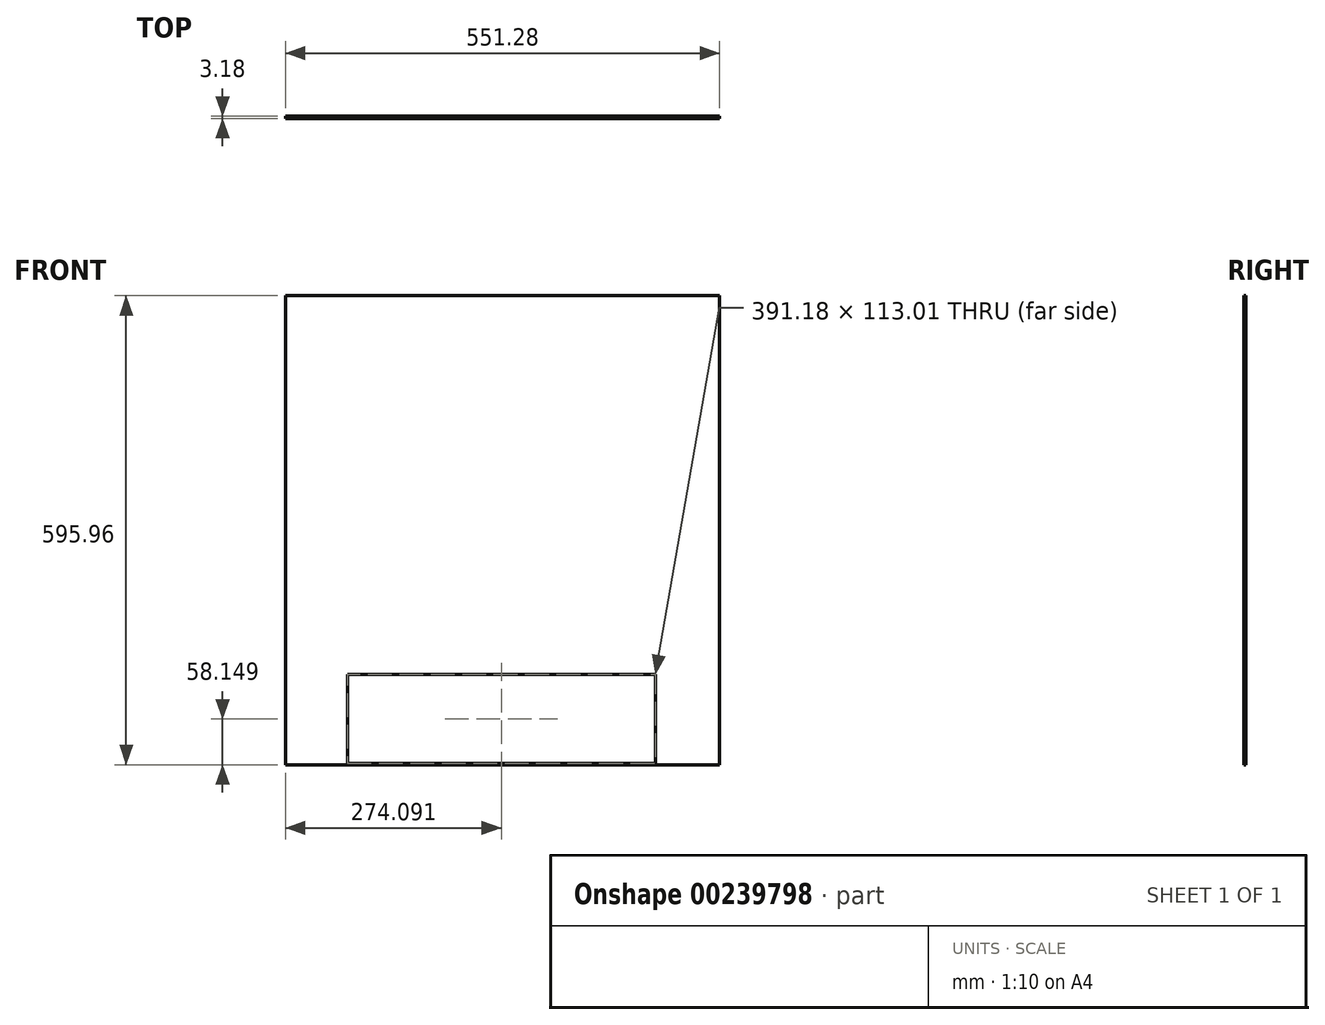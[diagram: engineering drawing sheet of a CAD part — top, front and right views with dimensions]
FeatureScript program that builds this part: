
annotation { "Feature Type Name" : "Feature", "Feature Type Description" : "" }
export const myFeature = defineFeature(function(context is Context, id is Id, definition is map)
    precondition{}
    {
        {
            var Q0;
            Q0=qCreatedBy(makeId("Front.planeOp"),FACE);
            var sketch = newSketch(context, id + "F0", { "sketchPlane" : qUnion([Q0])});
            skLineSegment(sketch, "E0.bottom", {"start": v(-92.42, -110.94) * mm, "end": v(458.86, -110.94) * mm});
            skLineSegment(sketch, "E0.top", {"start": v(-92.42, 485.02) * mm, "end": v(458.86, 485.02) * mm});
            skLineSegment(sketch, "E0.left", {"start": v(-92.42, -110.94) * mm, "end": v(-92.42, 485.02) * mm});
            skLineSegment(sketch, "E0.right", {"start": v(458.86, -110.94) * mm, "end": v(458.86, 485.02) * mm});
            skSolve(sketch);
        }
        {
            var Q0;
            Q0=makeQuery(id+"F0.imprint","IMPRINT",FACE,{"disambiguationData":[TD([[makeQuery(id+"F0.imprint","IMPRINT",EDGE,{"derivedFrom":sQuery(id+"F0.wireOp",EDGE,"E0.bottom")}),1.0]])]});
            var sketch = newSketch(context, id + "F1", { "sketchPlane" : qUnion([Q0])});
            skLineSegment(sketch, "E1.bottom", {"start": v(377.26, 3.71) * mm, "end": v(-13.92, 3.71) * mm});
            skLineSegment(sketch, "E1.top", {"start": v(377.26, -109.3) * mm, "end": v(-13.92, -109.3) * mm});
            skLineSegment(sketch, "E1.left", {"start": v(377.26, 3.71) * mm, "end": v(377.26, -109.3) * mm});
            skLineSegment(sketch, "E1.right", {"start": v(-13.92, 3.71) * mm, "end": v(-13.92, -109.3) * mm});
            skPoint(sketch, "E1.middle", {"position": v(181.67, -52.8) * mm});
            skSolve(sketch);
        }
        {
            var Q0;
            Q0 = qSketchRegion(id + "F0", true);
            extrude(context, id + "F2", {"entities" : qUnion([Q0]), "depth" : 3.17 * mm});
        }
        {
            var Q0;
            Q0 = qSketchRegion(id + "F1", true);
            extrude(context, id + "F3", {"entities" : qUnion([Q0]), "operationType" : NewBodyOperationType.REMOVE, "depth" : 25.4 * mm, "hasSecondDirection" : true, "secondDirectionOppositeDirection" : true, "secondDirectionDepth" : 25.4 * mm});
        }
    });
